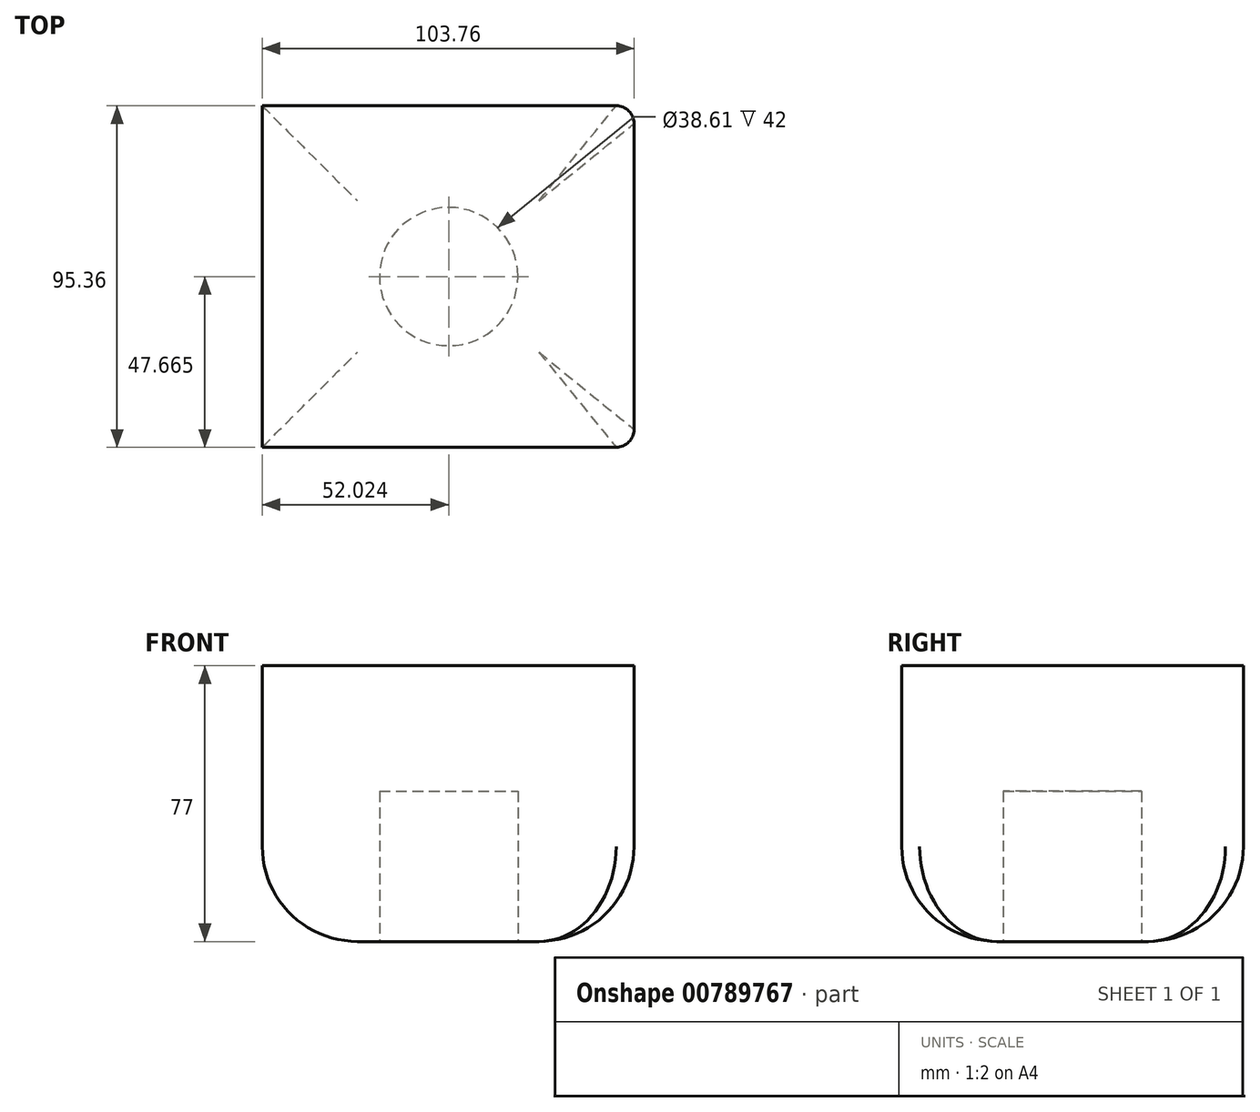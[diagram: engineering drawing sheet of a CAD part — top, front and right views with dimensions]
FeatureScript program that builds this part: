
annotation { "Feature Type Name" : "Feature", "Feature Type Description" : "" }
export const myFeature = defineFeature(function(context is Context, id is Id, definition is map)
    precondition{}
    {
        {
            var Q0;
            Q0=qCreatedBy(makeId("Top.planeOp"),FACE);
            var sketch = newSketch(context, id + "F0", { "sketchPlane" : qUnion([Q0])});
            skLineSegment(sketch, "E0", {"start": v(48.07, 43.18) * mm, "end": v(-55.7, 43.18) * mm});
            skLineSegment(sketch, "E1", {"start": v(-55.7, 43.18) * mm, "end": v(-55.7, -52.18) * mm});
            skLineSegment(sketch, "E2", {"start": v(-55.7, -52.18) * mm, "end": v(51.1, -52.18) * mm});
            skLineSegment(sketch, "E3", {"start": v(48.07, 43.18) * mm, "end": v(48.07, -52.18) * mm});
            skSolve(sketch);
        }
        {
            var Q0;
            Q0=makeQuery(id+"F0.imprint","IMPRINT",FACE,{"disambiguationData":[TD([[makeQuery(id+"F0.imprint","IMPRINT",EDGE,{"derivedFrom":sQuery(id+"F0.wireOp",EDGE,"E0")}),1.0]])]});
            extrude(context, id + "F1", {"entities" : qUnion([Q0]), "depth" : 77 * mm, "offsetDistance" : 25 * mm});
        }
        {
            var Q0;
            Q0=makeQuery(id+"F1.opExtrude","CAP_EDGE",EDGE,{"disambiguationData":[OSD([sQuery(id+"F0.wireOp",EDGE,"E0")])],"isStart":true});
            var Q1;
            Q1=makeQuery(id+"F1.opExtrude","CAP_EDGE",EDGE,{"disambiguationData":[OSD([sQuery(id+"F0.wireOp",EDGE,"E3")])],"isStart":true});
            var Q2;
            Q2=makeQuery(id+"F1.opExtrude","CAP_EDGE",EDGE,{"disambiguationData":[OSD([sQuery(id+"F0.wireOp",EDGE,"E2")])],"isStart":true});
            var Q3;
            Q3=makeQuery(id+"F1.opExtrude","CAP_EDGE",EDGE,{"disambiguationData":[OSD([sQuery(id+"F0.wireOp",EDGE,"E1")])],"isStart":true});
            fillet(context, id + "F2", {"entities" : qUnion([Q0, Q1, Q2, Q3]), "radius" : 26.56 * mm, "tangentPropagation" : true, "allowEdgeOverflow" : false});
        }
        {
            var Q0;
            Q0=makeQuery(id+"F1.opExtrude","CAP_FACE",FACE,{"disambiguationData":[OSD([sQuery(id+"F0.wireOp",EDGE,"E0"),sQuery(id+"F0.wireOp",EDGE,"E1"),sQuery(id+"F0.wireOp",EDGE,"E2"),sQuery(id+"F0.wireOp",EDGE,"E3")])],"isStart":true});
            var sketch = newSketch(context, id + "F3", { "sketchPlane" : qUnion([Q0])});
            skCircle(sketch, "E4", {"center": v(-3.67, 4.51) * mm, "radius": 19.3 * mm});
            skSolve(sketch);
        }
        {
            var Q0;
            Q0=makeQuery(id+"F3.imprint","IMPRINT",FACE,{"disambiguationData":[TD([[makeQuery(id+"F3.imprint","IMPRINT",EDGE,{"derivedFrom":sQuery(id+"F3.wireOp",EDGE,"E4")}),1.0]])]});
            extrude(context, id + "F4", {"entities" : qUnion([Q0]), "operationType" : NewBodyOperationType.REMOVE, "oppositeDirection" : true, "depth" : 42 * mm, "offsetDistance" : 25 * mm});
        }
        {
            var Q0;
            Q0=makeQuery(id+"F1.opExtrude","SWEPT_EDGE",EDGE,{"disambiguationData":[OSD([sQuery(id+"F0.wireOp",EDGE,"E0"),sQuery(id+"F0.wireOp",EDGE,"E3")])]});
            var Q1;
            Q1=makeQuery(id+"F1.opExtrude","SWEPT_EDGE",EDGE,{"disambiguationData":[OSD([sQuery(id+"F0.wireOp",EDGE,"E2"),sQuery(id+"F0.wireOp",EDGE,"E3")])]});
            fillet(context, id + "F5", {"entities" : qUnion([Q0, Q1]), "radius" : 5 * mm, "tangentPropagation" : true, "allowEdgeOverflow" : false});
        }
    });
